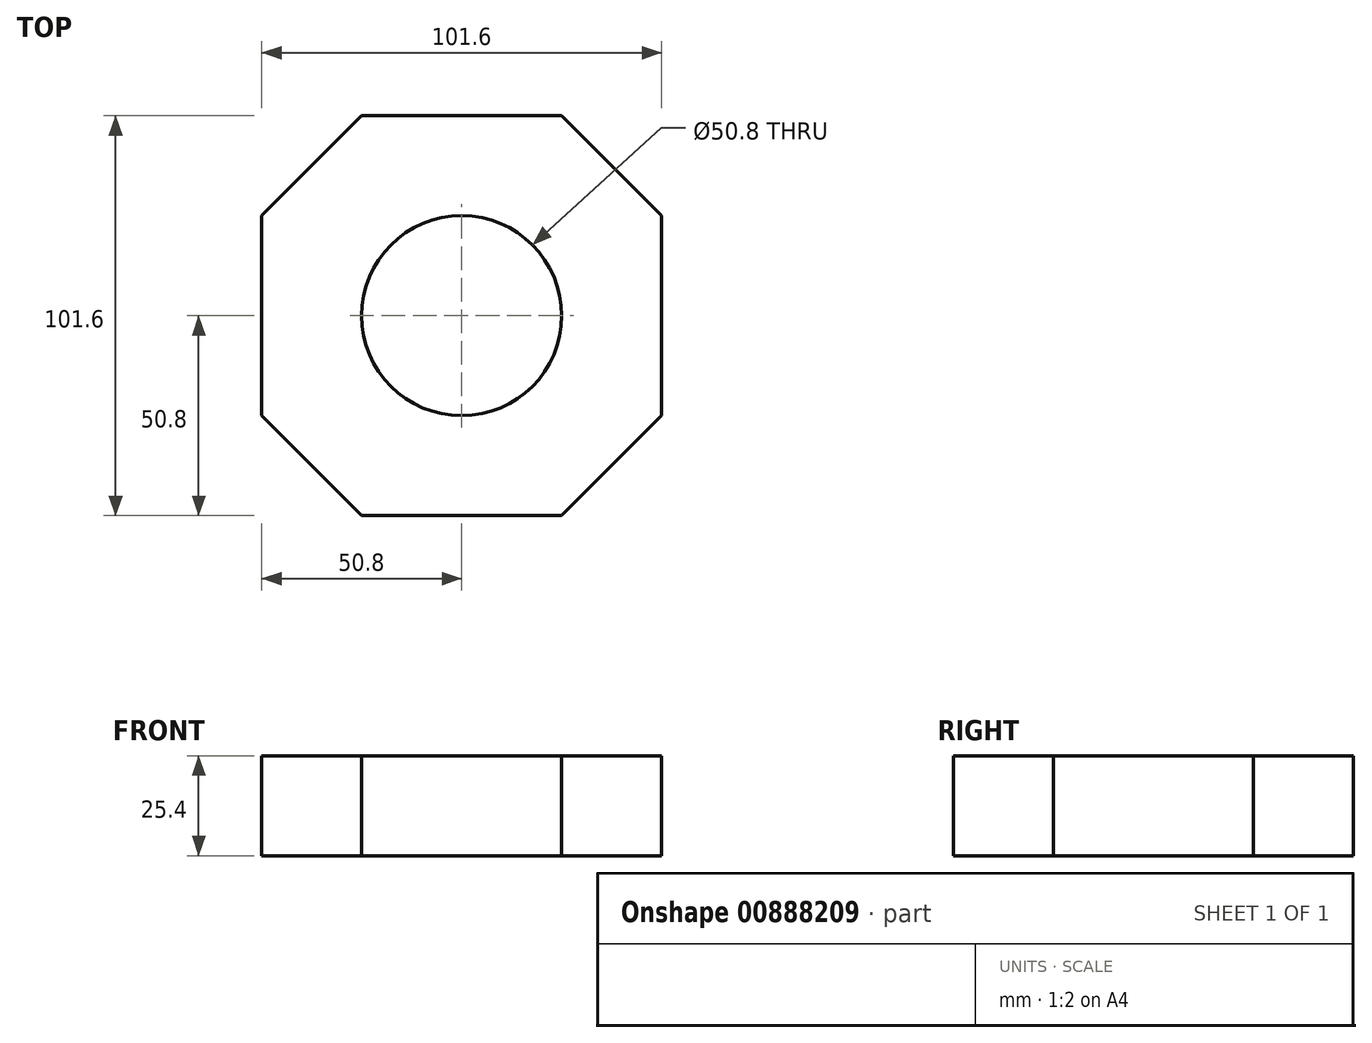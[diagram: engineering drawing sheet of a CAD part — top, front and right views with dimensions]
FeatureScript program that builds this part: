
annotation { "Feature Type Name" : "Feature", "Feature Type Description" : "" }
export const myFeature = defineFeature(function(context is Context, id is Id, definition is map)
    precondition{}
    {
        {
            var Q0;
            Q0=qCreatedBy(makeId("Top.planeOp"),FACE);
            var sketch = newSketch(context, id + "F0", { "sketchPlane" : qUnion([Q0])});
            skLineSegment(sketch, "E0.left", {"start": v(-50.8, -25.4) * mm, "end": v(-50.8, 25.4) * mm});
            skLineSegment(sketch, "E0.right", {"start": v(50.8, -25.4) * mm, "end": v(50.8, 25.4) * mm});
            skPoint(sketch, "E0.middle", {"position": v(0, 0) * mm});
            skLineSegment(sketch, "E1.bottom", {"start": v(-25.4, -50.8) * mm, "end": v(25.4, -50.8) * mm});
            skLineSegment(sketch, "E1.top", {"start": v(-25.4, 50.8) * mm, "end": v(25.4, 50.8) * mm});
            skLineSegment(sketch, "E2", {"start": v(25.4, -50.8) * mm, "end": v(50.8, -25.4) * mm});
            skLineSegment(sketch, "E3", {"start": v(-25.4, -50.8) * mm, "end": v(-50.8, -25.4) * mm});
            skLineSegment(sketch, "E4", {"start": v(-50.8, 25.4) * mm, "end": v(-25.4, 50.8) * mm});
            skLineSegment(sketch, "E5", {"start": v(25.4, 50.8) * mm, "end": v(50.8, 25.4) * mm});
            skSolve(sketch);
        }
        {
            var Q0;
            Q0=makeQuery(id+"F0.imprint","IMPRINT",FACE,{"disambiguationData":[TD([[makeQuery(id+"F0.imprint","IMPRINT",EDGE,{"derivedFrom":sQuery(id+"F0.wireOp",EDGE,"E0.left")}),-1.0]])]});
            extrude(context, id + "F1", {"entities" : qUnion([Q0]), "depth" : 25.4 * mm, "offsetDistance" : 25.4 * mm});
        }
        {
            var Q0;
            Q0=makeQuery(id+"F1.opExtrude","CAP_FACE",FACE,{"disambiguationData":[OSD([sQuery(id+"F0.wireOp",EDGE,"E0.left"),sQuery(id+"F0.wireOp",EDGE,"E0.right"),sQuery(id+"F0.wireOp",EDGE,"E1.bottom"),sQuery(id+"F0.wireOp",EDGE,"E1.top"),sQuery(id+"F0.wireOp",EDGE,"E2"),sQuery(id+"F0.wireOp",EDGE,"E3"),sQuery(id+"F0.wireOp",EDGE,"E4"),sQuery(id+"F0.wireOp",EDGE,"E5")])],"isStart":false});
            var sketch = newSketch(context, id + "F2", { "sketchPlane" : qUnion([Q0])});
            skCircle(sketch, "E6", {"center": v(0, 0) * mm, "radius": 25.4 * mm});
            skSolve(sketch);
        }
        {
            var Q0;
            Q0=makeQuery(id+"F2.imprint","IMPRINT",FACE,{"disambiguationData":[TD([[makeQuery(id+"F2.imprint","IMPRINT",EDGE,{"derivedFrom":sQuery(id+"F2.wireOp",EDGE,"E6")}),1.0]])]});
            extrude(context, id + "F3", {"entities" : qUnion([Q0]), "operationType" : NewBodyOperationType.REMOVE, "oppositeDirection" : true, "depth" : 25.4 * mm, "offsetDistance" : 25.4 * mm});
        }
    });
